# Revit family: IVLB_L4U_LF_Track Spot - EDDA S
name_source: partatom
category: Lighting Fixtures
units: mm (PartAtom-declared; Revit-internal decimal feet)

## family parameters
Always vertical = No
Cut with Voids When Loaded = No
Light Source = No
Part Type = Normal
Room Calculation Point = No
Round Connector Dimension = Use Diameter
Shared = No
Work Plane-Based = No

## types (8) — shared parameters
Assembly Code = 63.00
Description = Track Spot Edda S
IfcExportAs = IfcLightFixtureType
IfcExportType = POINTSOURCE
Lamp = LED
Manufacturer = Light4U
Model = Track Spot Edda S
Track Adapter_Height = 30 mm  [stored 0.0984252 ft]
Track Adapter_Length = 228 mm  [stored 0.748031 ft]
Track Adapter_Width = 29 mm  [stored 0.0951444 ft]
Track_Spot_Diameter = 85 mm  [stored 0.278871 ft]
Track_Spot_Length = 104 mm  [stored 0.341207 ft]
Track_Spot_Position_LR = 55 mm  [stored 0.180446 ft]
Type Comments = Edda S
URL = https://light4u.io
⌂ Powered by IVLibrary = www.ivlibrary.com

## per-type parameters (varying)
| type | Apparent Load | Calc_Coupling_Length | Light Source | Track_Spot_Position_UD | Wattage Comments |
| EDDA S 1450lm_930 14W 15deg | 14 VA | 41 mm  [stored 0.134514 ft] | Lightsource S : EDDA S 1450lm_930 14W 15deg_LDT | 41 mm  [stored 0.134514 ft] | 14W |
| EDDA S 1450lm_930 14W 24deg | 14 VA | 41 mm  [stored 0.134514 ft] | Lightsource S : EDDA S 1450lm_930 14W 24deg_LDT | 41 mm  [stored 0.134514 ft] | 14W |
| EDDA S 1450lm_930 14W 45deg | 14 VA | 41 mm  [stored 0.134514 ft] | Lightsource S : EDDA S 1450lm_930 14W 45deg_LDT | 41 mm  [stored 0.134514 ft] | 14W |
| EDDA S 1450lm_930 14W 55deg | 14 VA | 41 mm  [stored 0.134514 ft] | Lightsource S : EDDA S 1450lm_930 14W 55deg_LDT | 41 mm  [stored 0.134514 ft] | 14W |
| EDDA S 2000lm_930 18.5W 15deg | 19 VA | 41 mm  [stored 0.134514 ft] | Lightsource S : EDDA S 2000lm_930 18.5W 15deg_LDT | 41 mm  [stored 0.134514 ft] | 18.5W |
| EDDA S 2000lm_930 18.5W 24deg | 19 VA | 41 mm  [stored 0.134514 ft] | Lightsource S : EDDA S 2000lm_930 18.5W 24deg_LDT | 41 mm  [stored 0.134514 ft] | 18.5W |
| EDDA S 2000lm_930 18.5W 45deg | 19 VA | 41 mm  [stored 0.134514 ft] | Lightsource S : EDDA S 2000lm_930 18.5W 45deg_LDT | 41 mm  [stored 0.134514 ft] | 18.5W |
| EDDA S 2000lm_930 18.5W 55deg | 19 VA | 45 mm  [stored 0.147638 ft] | Lightsource S : EDDA S 2000lm_930 18.5W 55deg_LDT | 45 mm  [stored 0.147638 ft] | 18.5W |

note: [stored X ft] marks values corroborated as IEEE doubles in the binary element streams (Revit-internal decimal feet)

## geometry (parser evidence)
native form markers: Sweep x18
no freeform markers — native parametric forms only
